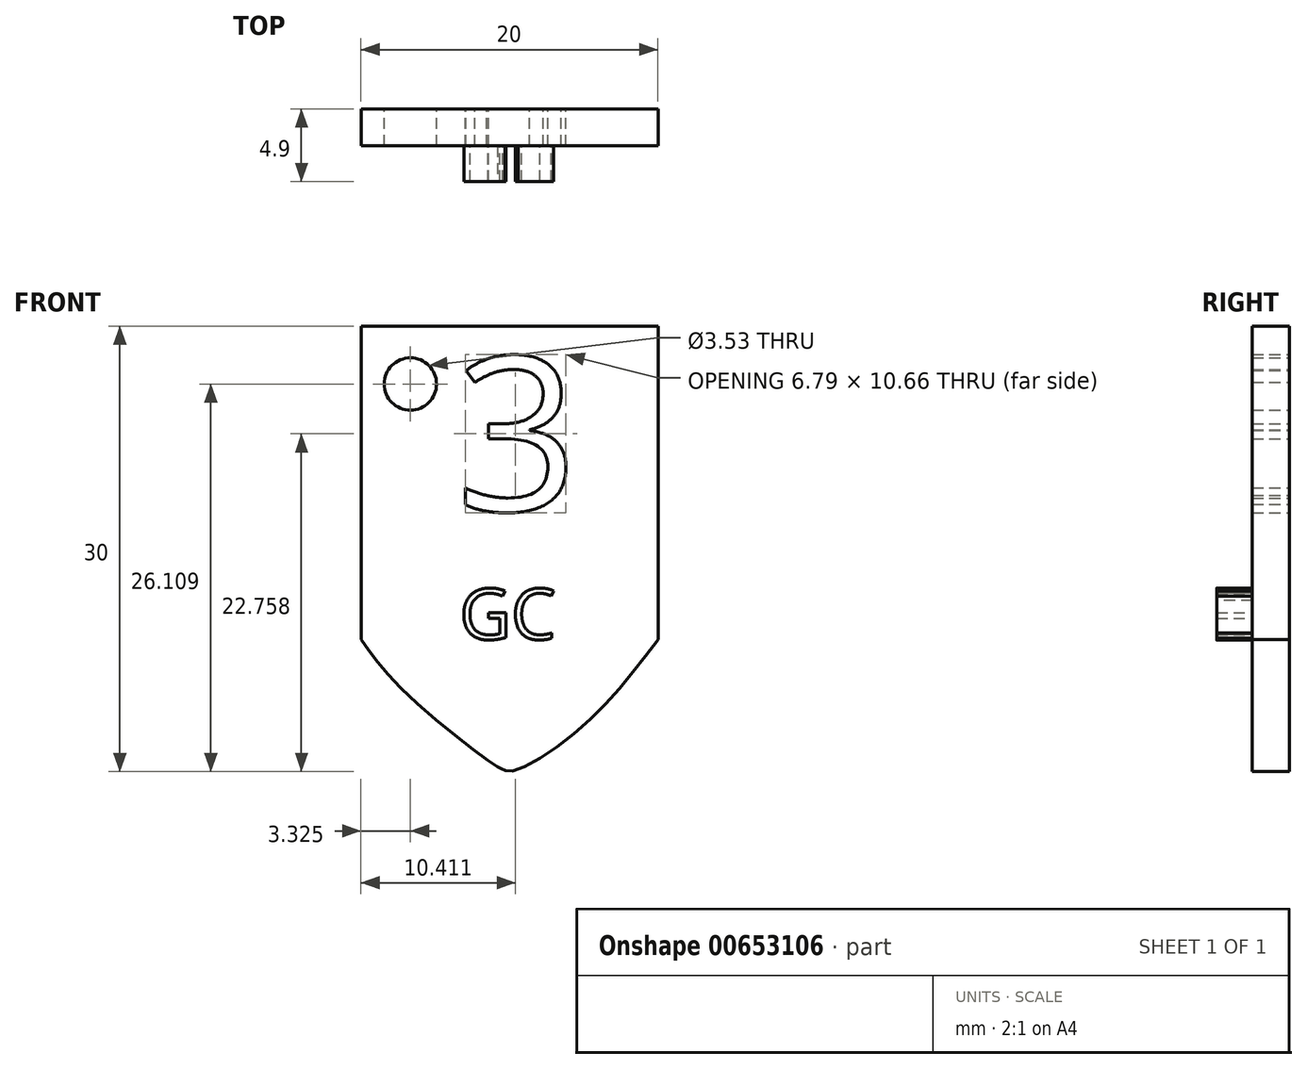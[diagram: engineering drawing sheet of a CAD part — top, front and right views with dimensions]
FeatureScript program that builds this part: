
annotation { "Feature Type Name" : "Feature", "Feature Type Description" : "" }
export const myFeature = defineFeature(function(context is Context, id is Id, definition is map)
    precondition{}
    {
        {
            var Q0;
            Q0=qCreatedBy(makeId("Front.planeOp"),FACE);
            var sketch = newSketch(context, id + "F0", { "sketchPlane" : qUnion([Q0])});
            skLineSegment(sketch, "E0", {"start": v(-29.07, 21.1) * mm, "end": v(-29.07, 0) * mm});
            skLineSegment(sketch, "E1", {"start": v(-29.07, 21.1) * mm, "end": v(-9.07, 21.1) * mm});
            skLineSegment(sketch, "E2", {"start": v(-9.07, 21.1) * mm, "end": v(-9.07, 0) * mm});
            skFitSpline(sketch, "E3", {"points": [v(-29.07, 0) * mm, v(-26.02, -3.64) * mm, v(-19.92, -8.56) * mm, v(-19.58, -8.73) * mm, v(-19.07, -8.9) * mm, v(-14.32, -6.02) * mm, v(-9.07, 0) * mm], "startDerivative": vector(11.94, -17.2) * mm, "endDerivative": vector(19.2, 25.6) * mm});
            skPoint(sketch, "E4", {"position": v(-19.07, 21.1) * mm});
            skPoint(sketch, "E5", {"position": v(-29.07, 8.58) * mm});
            skPoint(sketch, "E6", {"position": v(-9.07, 8.58) * mm});
            skSolve(sketch);
        }
        {
            var Q0;
            Q0 = qSketchRegion(id + "F0", true);
            extrude(context, id + "F1", {"entities" : qUnion([Q0]), "depth" : 2.5 * mm, "offsetDistance" : 25 * mm});
        }
        {
            var Q0;
            Q0=qCreatedBy(makeId("Front.planeOp"),FACE);
            var sketch = newSketch(context, id + "F2", { "sketchPlane" : qUnion([Q0])});
            skText(sketch, "E7", { "text": "3\n", "fontName": "OpenSans-Regular.ttf"});
            const initialGuessF2  = {"E7": [-0.02272, 0.00867, 1, 0, 0.01046]};
            skSetInitialGuess(sketch, initialGuessF2);
            skSolve(sketch);
        }
        {
            var Q0;
            Q0 = qSketchRegion(id + "F2", true);
            extrude(context, id + "F3", {"entities" : qUnion([Q0]), "operationType" : NewBodyOperationType.REMOVE, "endBound" : BoundingType.UP_TO_NEXT, "depth" : 25 * mm, "offsetDistance" : 25 * mm});
        }
        {
            var Q0;
            Q0=qCreatedBy(makeId("Front.planeOp"),FACE);
            var sketch = newSketch(context, id + "F4", { "sketchPlane" : qUnion([Q0])});
            skText(sketch, "E8", { "text": "GC", "fontName": "OpenSans-Regular.ttf"});
            const initialGuessF4  = {"E8": [-0.02244, 0, 1, 0, 0.00344]};
            skSetInitialGuess(sketch, initialGuessF4);
            skSolve(sketch);
        }
        {
            var Q0;
            Q0 = qSketchRegion(id + "F4", true);
            extrude(context, id + "F5", {"entities" : qUnion([Q0]), "operationType" : NewBodyOperationType.ADD, "depth" : 4.9 * mm, "offsetDistance" : 25 * mm});
        }
        {
            var Q0;
            Q0=qCreatedBy(makeId("Front.planeOp"),FACE);
            var sketch = newSketch(context, id + "F6", { "sketchPlane" : qUnion([Q0])});
            skCircle(sketch, "E9", {"center": v(-25.75, 17.2) * mm, "radius": 1.76 * mm});
            skSolve(sketch);
        }
        {
            var Q0;
            Q0 = qSketchRegion(id + "F6", true);
            extrude(context, id + "F7", {"entities" : qUnion([Q0]), "operationType" : NewBodyOperationType.REMOVE, "endBound" : BoundingType.UP_TO_NEXT, "depth" : 25 * mm, "offsetDistance" : 25 * mm});
        }
    });
